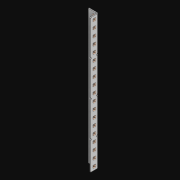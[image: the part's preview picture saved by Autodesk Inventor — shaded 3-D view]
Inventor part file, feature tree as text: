
AUTODESK INVENTOR PART (.ipt)
format: ipt  version: 2021 (Build 250183000, 183)  size: 1,201,152 bytes
history: native  units: in
note: dims shown in document units (in); Inventor stores cm internally (conversion verified against a paired STEP export)
features: extrude x40, other x38, sketch x4, pattern_linear x2, sheet_metal_op x1
ambient origin geometry x8: Origin, YZ Plane, XZ Plane, XY Plane, X Axis, Y Axis, Z Axis, Center Point
bodies: Solid1 (feature_tree)
feature tree (85):
  pattern_linear  "Rectangular Pattern1"  Spacing1=0.5in  [1 undecoded]
  pattern_linear  "Rectangular Pattern3"  Count1=19  [1 undecoded]
  extrude  "Extrusion1"  Depth=0.5in
  extrude  "Extrusion2"  Depth=0.5in
  sketch  "Sketch1"  dims[d0=0.182in]
  other  "Srf1"
  sketch  "Sketch3"  dims[d1=0.063in d2=0.0in]
  other  "Srf3"
  other  "Srf4"
  other  "Srf5"
  other  "Srf6"
  other  "Srf7"
  other  "Srf8"
  other  "Srf9"
  other  "Srf10"
  other  "Srf11"
  other  "Srf12"
  other  "Srf13"
  other  "Srf14"
  other  "Srf15"
  other  "Srf16"
  other  "Srf17"
  other  "Srf18"
  other  "Srf19"
  other  "Srf20"
  other  "Srf21"
  other  "Srf142"
  other  "Srf143"
  other  "Srf144"
  other  "Srf145"
  other  "Srf146"
  other  "Srf147"
  other  "Srf148"
  other  "Srf149"
  other  "Srf150"
  other  "Srf151"
  other  "Srf152"
  other  "Srf153"
  other  "Srf154"
  other  "Srf155"
  other  "Srf156"
  other  "Srf157"
  other  "Srf158"
  other  "Srf159"
  sketch  "Sketch4"  dims[d6=0.182in]
  sketch  "Sketch5"  dims[d7=0.063in d8=0.0in d11=0.5in d12=0.3937in d14=0.5in d18=7.4803in d20=0.5in d21=8.0in d22=0.0in d23=0.841in d24=0.0in]
  sheet_metal_op  "Fold1"
  extrude  "ExtrusionSrf1"  TaperAngle=0.0deg  [1 undecoded]
  extrude  "ExtrusionSrf3"  Depth=0.5in TaperAngle=0.0deg
  extrude  "ExtrusionSrf4"  [1 undecoded]
  extrude  "ExtrusionSrf5"  [1 undecoded]
  extrude  "ExtrusionSrf6"  [1 undecoded]
  extrude  "ExtrusionSrf7"  [1 undecoded]
  extrude  "ExtrusionSrf8"  [1 undecoded]
  extrude  "ExtrusionSrf9"  [1 undecoded]
  extrude  "ExtrusionSrf10"  [1 undecoded]
  extrude  "ExtrusionSrf11"  [1 undecoded]
  extrude  "ExtrusionSrf12"  [1 undecoded]
  extrude  "ExtrusionSrf13"  [1 undecoded]
  extrude  "ExtrusionSrf14"  [1 undecoded]
  extrude  "ExtrusionSrf15"  [1 undecoded]
  extrude  "ExtrusionSrf16"  [1 undecoded]
  extrude  "ExtrusionSrf17"  [1 undecoded]
  extrude  "ExtrusionSrf18"  [1 undecoded]
  extrude  "ExtrusionSrf19"  [1 undecoded]
  extrude  "ExtrusionSrf20"  [1 undecoded]
  extrude  "ExtrusionSrf21"  [1 undecoded]
  extrude  "ExtrusionSrf142"  [1 undecoded]
  extrude  "ExtrusionSrf143"  [1 undecoded]
  extrude  "ExtrusionSrf144"  [1 undecoded]
  extrude  "ExtrusionSrf145"  [1 undecoded]
  extrude  "ExtrusionSrf146"  [1 undecoded]
  extrude  "ExtrusionSrf147"  [1 undecoded]
  extrude  "ExtrusionSrf148"  [1 undecoded]
  extrude  "ExtrusionSrf149"  [1 undecoded]
  extrude  "ExtrusionSrf150"  [1 undecoded]
  extrude  "ExtrusionSrf151"  [1 undecoded]
  extrude  "ExtrusionSrf152"  [1 undecoded]
  extrude  "ExtrusionSrf153"  [1 undecoded]
  extrude  "ExtrusionSrf154"  [1 undecoded]
  extrude  "ExtrusionSrf155"  [1 undecoded]
  extrude  "ExtrusionSrf156"  [1 undecoded]
  extrude  "ExtrusionSrf157"  [1 undecoded]
  extrude  "ExtrusionSrf158"  [1 undecoded]
  extrude  "ExtrusionSrf159"  [1 undecoded]
note: 39 required parameter values undecoded (feature->parameter linkage not recoverable at this tier; creation-order binding heuristic only, values carry confidence <= 0.55)
